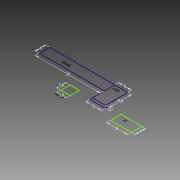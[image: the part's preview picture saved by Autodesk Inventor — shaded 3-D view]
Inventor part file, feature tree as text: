
AUTODESK INVENTOR PART (.ipt)
format: ipt  version: 2013 SP1 (Build 170176100, 176)  size: 73,216 bytes
history: native  units: mm
features: sketch x1
ambient origin geometry x8: Origin, YZ Plane, XZ Plane, XY Plane, X Axis, Y Axis, Z Axis, Center Point
feature tree (1):
  sketch  "Skizze1"  dims[d0=5.0mm d1=8.6mm d2=6.0mm d3=1.0mm d4=3.6mm d5=3.6mm d6=25.0mm d7=4.0mm d8=8.0mm d9=4.0mm]
